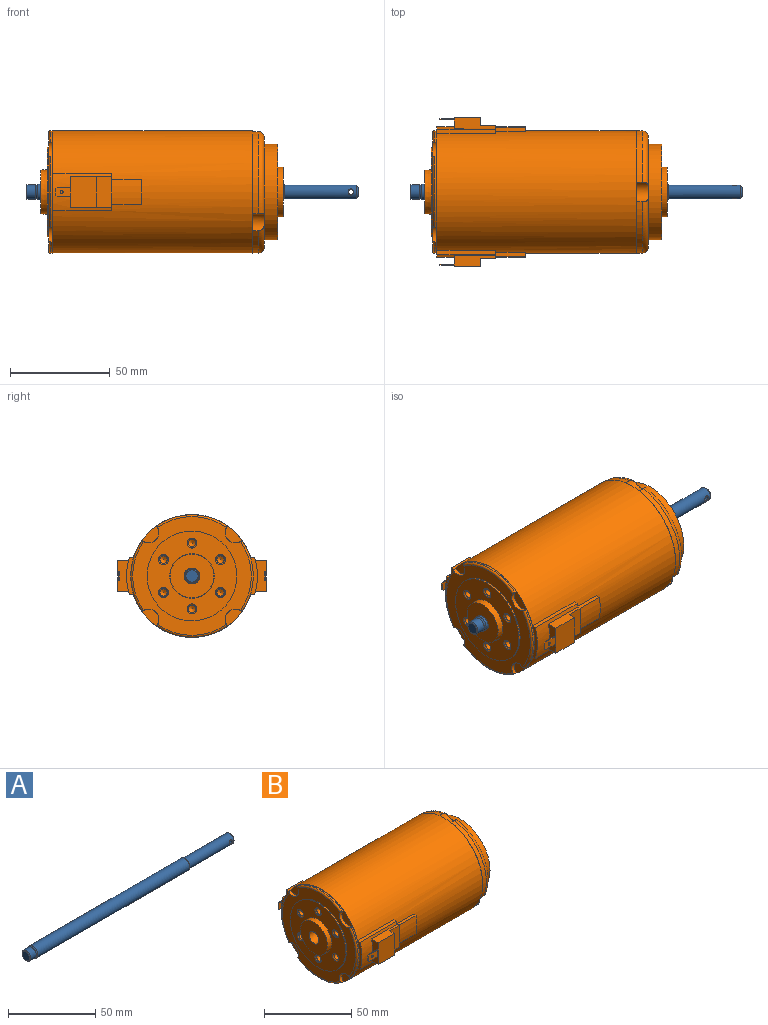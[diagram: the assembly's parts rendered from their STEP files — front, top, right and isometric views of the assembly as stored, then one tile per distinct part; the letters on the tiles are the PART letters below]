
ASSEMBLY  parts=2 mates=1
PART A: 12 faces, bbox 166.5x8.7x8.7 mm
  f0: cylinder r=3.5mm len=36mm, axis (-1,0,0), area 777.4mm2, adj f2,f4,f5,f11
  f1: plane 5x5mm, normal (1,0,0), area 19.6mm2, adj f2
  f2: cone r=2.5mm half-angle=45deg, axis (-1,0,0), area 26.7mm2, adj f0,f1
  f3: cylinder r=1.24mm len=5.92mm, axis (0,-1,0), area 46.1mm2, adj f4,f5
  f4: bspline ~3.07x2.89mm, area 2.8mm2, adj f0,f3
  f5: bspline ~3.07x2.89mm, area 2.8mm2, adj f0,f3
  f6: cylinder r=4mm len=123.2mm, axis (1,0,0), area 3096.4mm2, adj f9,f11
  f7: cylinder r=3.55mm len=7.1mm, axis (1,0,0), area 100.4mm2, adj f9,f10
  f8: plane 6.1x6.1mm, normal (-1,0,0), area 29.2mm2, adj f10
  f9: cone r=3.55mm half-angle=29.4deg, axis (1,0,0), area 21.8mm2, adj f6,f7
  f10: cone r=3.05mm half-angle=45deg, axis (1,0,0), area 14.7mm2, adj f7,f8
  f11: torus R=4mm, axis (-1,0,0), area 18.2mm2, adj f0,f6
PART B: 105 faces, bbox 121.7x74.3x66.6 mm
  f0: cylinder r=30.75mm len=35.59mm, axis (1,0,0), area 38mm2, adj f1,f18,f35,f54
  f1: cylinder r=5.17mm len=8.49mm, axis (-1,0,0), area 30.2mm2, adj f0,f2,f18,f20,f54,f55
  f2: cylinder r=30.75mm len=35.59mm, axis (1,0,0), area 38mm2, adj f1,f3,f18,f55
  f3: cylinder r=5.17mm len=8.49mm, axis (-1,0,0), area 30.2mm2, adj f2,f4,f18,f20,f55,f56
  f4: cylinder r=30.75mm len=35.59mm, axis (1,0,0), area 38mm2, adj f3,f5,f18,f56
  f5: cylinder r=5.17mm len=8.49mm, axis (-1,0,0), area 30.2mm2, adj f4,f6,f18,f20,f56,f57
  f6: cylinder r=30.75mm len=35.59mm, axis (1,0,0), area 38mm2, adj f5,f18,f35,f57
  f7: cylinder r=30.62mm len=47.52mm, axis (1,0,0), area 163.2mm2, adj f8,f10,f19,f58
  f8: cylinder r=5.09mm len=8.52mm, axis (1,0,0), area 73mm2, adj f7,f11,f12,f19,f58,f60
  f9: cylinder r=30.62mm len=41.16mm, axis (1,0,0), area 163.2mm2, adj f10,f19,f34,f59
  f10: cylinder r=5.09mm len=8.52mm, axis (1,0,0), area 73mm2, adj f7,f9,f12,f19,f58,f59
  f11: cylinder r=30.62mm len=41.16mm, axis (1,0,0), area 163.2mm2, adj f8,f19,f34,f60
  f12: plane 55.25x55.12mm, normal (1,0,0), area 585.2mm2, adj f8,f10,f15,f34,f58,f59,f60
  f13: cylinder r=12.5mm len=25mm, axis (1,0,0), area 223.8mm2, adj f14,f16
  f14: plane 25x25mm, normal (1,0,0), area 440.6mm2, adj f13,f25
  f15: cylinder r=23.95mm len=47.9mm, axis (1,0,0), area 1008.2mm2, adj f12,f16
  f16: plane 47.9x47.9mm, normal (1,0,0), area 1258.3mm2, adj f13,f15,f26,f28,f30,f32
  f17: cylinder r=30.8mm len=100mm, axis (1,0,0), area 17825.8mm2, adj f18,f19,f62,f64,f65,f67,f68,f69
  f18: plane 65.6x61.6mm, normal (-1,0,0), area 248mm2, adj f0,f1,f2,f3,f4,f5,f6,f17
  f19: plane 61.6x61.6mm, normal (1,0,0), area 116.8mm2, adj f7,f8,f9,f10,f11,f17,f34
  f20: plane 59.5x59.5mm, normal (-1,0,0), area 1069.7mm2, adj f1,f3,f5,f21,f35,f54,f55,f56
  f21: cylinder r=22.5mm len=45mm, axis (1,0,0), area 113.1mm2, adj f20,f22
  f22: plane 45x45mm, normal (-1,0,0), area 1082.1mm2, adj f21,f23,f38,f41,f44,f47,f50,f53
  f23: cone r=11.15mm half-angle=3deg, axis (1,0,0), area 229.7mm2, adj f22,f24
  f24: plane 21.95x21.95mm, normal (-1,0,0), area 328.3mm2, adj f23,f25
  f25: cylinder r=4mm len=121.65mm, axis (1,0,0), area 3057.4mm2, adj f14,f24
  f26: cylinder r=2.05mm len=5.3mm, axis (1,0,0), area 68.3mm2, adj f16,f27
  f27: cone r=0mm half-angle=59deg, axis (1,0,0), area 15.4mm2, adj f26
  f28: cylinder r=2.05mm len=5.3mm, axis (1,0,0), area 68.3mm2, adj f16,f29
  f29: cone r=0mm half-angle=59deg, axis (1,0,0), area 15.4mm2, adj f28
  f30: cylinder r=2.05mm len=5.3mm, axis (1,0,0), area 68.3mm2, adj f16,f31
  f31: cone r=0mm half-angle=59deg, axis (1,0,0), area 15.4mm2, adj f30
  f32: cylinder r=2.05mm len=5.3mm, axis (1,0,0), area 68.3mm2, adj f16,f33
  f33: cone r=0mm half-angle=59deg, axis (1,0,0), area 15.4mm2, adj f32
  f34: cylinder r=5.09mm len=9.7mm, axis (1,0,0), area 73mm2, adj f9,f11,f12,f19,f59,f60
  f35: cylinder r=5.17mm len=8.49mm, axis (-1,0,0), area 30.2mm2, adj f0,f6,f18,f20,f54,f57
  f36: cone r=0mm half-angle=59deg, axis (-1,0,0), area 12.5mm2, adj f37
  f37: cylinder r=1.85mm len=5.25mm, axis (-1,0,0), area 61mm2, adj f36,f38
  f38: cone r=1.85mm half-angle=45deg, axis (-1,0,0), area 12.6mm2, adj f22,f37
  f39: cone r=0mm half-angle=59deg, axis (-1,0,0), area 12.5mm2, adj f40
  f40: cylinder r=1.85mm len=5.25mm, axis (-1,0,0), area 61mm2, adj f39,f41
  f41: cone r=1.85mm half-angle=45deg, axis (-1,0,0), area 12.6mm2, adj f22,f40
  f42: cone r=0mm half-angle=59deg, axis (-1,0,0), area 12.5mm2, adj f43
  f43: cylinder r=1.85mm len=5.25mm, axis (-1,0,0), area 61mm2, adj f42,f44
  f44: cone r=1.85mm half-angle=45deg, axis (-1,0,0), area 12.6mm2, adj f22,f43
  f45: cone r=0mm half-angle=59deg, axis (-1,0,0), area 12.5mm2, adj f46
  f46: cylinder r=1.85mm len=5.25mm, axis (-1,0,0), area 61mm2, adj f45,f47
  f47: cone r=1.85mm half-angle=45deg, axis (-1,0,0), area 12.6mm2, adj f22,f46
  f48: cone r=0mm half-angle=59deg, axis (-1,0,0), area 12.5mm2, adj f49
  f49: cylinder r=1.85mm len=5.25mm, axis (-1,0,0), area 61mm2, adj f48,f50
  f50: cone r=1.85mm half-angle=45deg, axis (-1,0,0), area 12.6mm2, adj f22,f49
  f51: cone r=0mm half-angle=59deg, axis (-1,0,0), area 12.5mm2, adj f52
  f52: cylinder r=1.85mm len=5.25mm, axis (-1,0,0), area 61mm2, adj f51,f53
  f53: cone r=1.85mm half-angle=45deg, axis (-1,0,0), area 12.6mm2, adj f22,f52
  f54: torus R=29.75mm, axis (-1,0,0), area 58.9mm2, adj f0,f1,f20,f35
  f55: torus R=29.75mm, axis (-1,0,0), area 58.9mm2, adj f1,f2,f3,f20
  f56: torus R=29.75mm, axis (-1,0,0), area 58.9mm2, adj f3,f4,f5,f20
  f57: torus R=29.75mm, axis (-1,0,0), area 58.9mm2, adj f5,f6,f20,f35
  f58: torus R=27.62mm, axis (-1,0,0), area 251.1mm2, adj f7,f8,f10,f12
  f59: torus R=27.62mm, axis (-1,0,0), area 251.1mm2, adj f9,f10,f12,f34
  f60: torus R=27.62mm, axis (-1,0,0), area 251.1mm2, adj f8,f11,f12,f34
  f61: plane 15.3x5.25mm, normal (-1,0,0), area 68.7mm2, adj f63,f66,f72,f73,f75,f76,f77,f78
  f62: plane 12.8x2.67mm, normal (1,0,0), area 25.8mm2, adj f17,f67,f69,f74
  f63: plane 20.8x5.25mm, normal (0,0,-1), area 81.6mm2, adj f61,f66,f68,f70,f71,f73
  f64: plane 29.5x2.1mm, normal (0,0,-1), area 61.8mm2, adj f17,f18,f68,f73
  f65: plane 29.5x2.1mm, normal (0,0,1), area 61.8mm2, adj f17,f18,f68,f73
  f66: plane 15.3x13.1mm, normal (0,1,0), area 200.4mm2, adj f61,f63,f70,f72
  f67: plane 15x2.04mm, normal (0,0,-1), area 30.6mm2, adj f17,f62,f68,f74
  f68: plane 19x4.25mm, normal (1,0,0), area 28.9mm2, adj f17,f63,f64,f65,f67,f69,f71,f72
  f69: plane 15x2.04mm, normal (0,0,1), area 30.6mm2, adj f17,f62,f68,f74
  f70: plane 15.3x3.6mm, normal (1,0,0), area 55.1mm2, adj f63,f66,f71,f72
  f71: plane 15.3x7.7mm, normal (0,1,0), area 117.8mm2, adj f63,f68,f70,f72
  f72: plane 20.8x5.25mm, normal (0,0,1), area 81.6mm2, adj f61,f66,f68,f70,f71,f73
  f73: cylinder r=32.8mm len=29.5mm, axis (-1,0,0), area 247.4mm2, adj f18,f61,f63,f64,f65,f68,f72
  f74: cylinder r=32.8mm len=15mm, axis (1,0,0), area 193.2mm2, adj f62,f67,f68,f69
  f75: plane 7.3x4.8mm, normal (0,-1,0), area 32.8mm2, adj f61,f76,f78,f79,f80,f81,f82
  f76: plane 6.6x0.5mm, normal (0,0,1), area 3.3mm2, adj f61,f75,f77,f80
  f77: plane 7.3x4.8mm, normal (0,1,0), area 32.8mm2, adj f61,f76,f78,f79,f80,f81,f82
  f78: plane 6.6x0.5mm, normal (0,0,-1), area 3.3mm2, adj f61,f75,f77,f81
  f79: plane 3.4x0.5mm, normal (-1,0,0), area 1.7mm2, adj f75,f77,f80,f81
  f80: plane 0.7x0.7mm, normal (-0.71,0,0.71), area 0.5mm2, adj f75,f76,f77,f79
  f81: plane 0.7x0.7mm, normal (-0.71,0,-0.71), area 0.5mm2, adj f75,f77,f78,f79
  f82: cylinder r=0.75mm len=1.5mm, axis (0,1,0), area 2.4mm2, adj f75,f77
  f83: plane 15.3x5.25mm, normal (-1,0,0), area 68.7mm2, adj f85,f88,f94,f95,f97,f98,f99,f100
  f84: plane 12.8x2.67mm, normal (1,0,0), area 25.8mm2, adj f17,f89,f91,f96
  f85: plane 20.8x5.25mm, normal (0,0,1), area 81.6mm2, adj f83,f88,f90,f92,f93,f95
  f86: plane 29.5x2.1mm, normal (0,0,1), area 61.8mm2, adj f17,f18,f90,f95
  f87: plane 29.5x2.1mm, normal (0,0,-1), area 61.8mm2, adj f17,f18,f90,f95
  f88: plane 15.3x13.1mm, normal (0,-1,0), area 200.4mm2, adj f83,f85,f92,f94
  f89: plane 15x2.04mm, normal (0,0,1), area 30.6mm2, adj f17,f84,f90,f96
  f90: plane 19x4.25mm, normal (1,0,0), area 28.9mm2, adj f17,f85,f86,f87,f89,f91,f93,f94
  f91: plane 15x2.04mm, normal (0,0,-1), area 30.6mm2, adj f17,f84,f90,f96
  f92: plane 15.3x3.6mm, normal (1,0,0), area 55.1mm2, adj f85,f88,f93,f94
  f93: plane 15.3x7.7mm, normal (0,-1,0), area 117.8mm2, adj f85,f90,f92,f94
  f94: plane 20.8x5.25mm, normal (0,0,-1), area 81.6mm2, adj f83,f88,f90,f92,f93,f95
  f95: cylinder r=32.8mm len=29.5mm, axis (-1,0,0), area 247.4mm2, adj f18,f83,f85,f86,f87,f90,f94
  f96: cylinder r=32.8mm len=15mm, axis (1,0,0), area 193.2mm2, adj f84,f89,f90,f91
  f97: plane 7.3x4.8mm, normal (0,1,0), area 32.8mm2, adj f83,f98,f100,f101,f102,f103,f104
  f98: plane 6.6x0.5mm, normal (0,0,-1), area 3.3mm2, adj f83,f97,f99,f102
  f99: plane 7.3x4.8mm, normal (0,-1,0), area 32.8mm2, adj f83,f98,f100,f101,f102,f103,f104
  f100: plane 6.6x0.5mm, normal (0,0,1), area 3.3mm2, adj f83,f97,f99,f103
  f101: plane 3.4x0.5mm, normal (-1,0,0), area 1.7mm2, adj f97,f99,f102,f103
  f102: plane 0.7x0.7mm, normal (-0.71,0,-0.71), area 0.5mm2, adj f97,f98,f99,f101
  f103: plane 0.7x0.7mm, normal (-0.71,0,0.71), area 0.5mm2, adj f97,f99,f100,f101
  f104: cylinder r=0.75mm len=1.5mm, axis (0,-1,0), area 2.4mm2, adj f97,f99
PLACE A at identity
PLACE B at identity
MATE revolute A.f0 <-> B.f0  axis (1,0,0) through (0,0,0)mm
